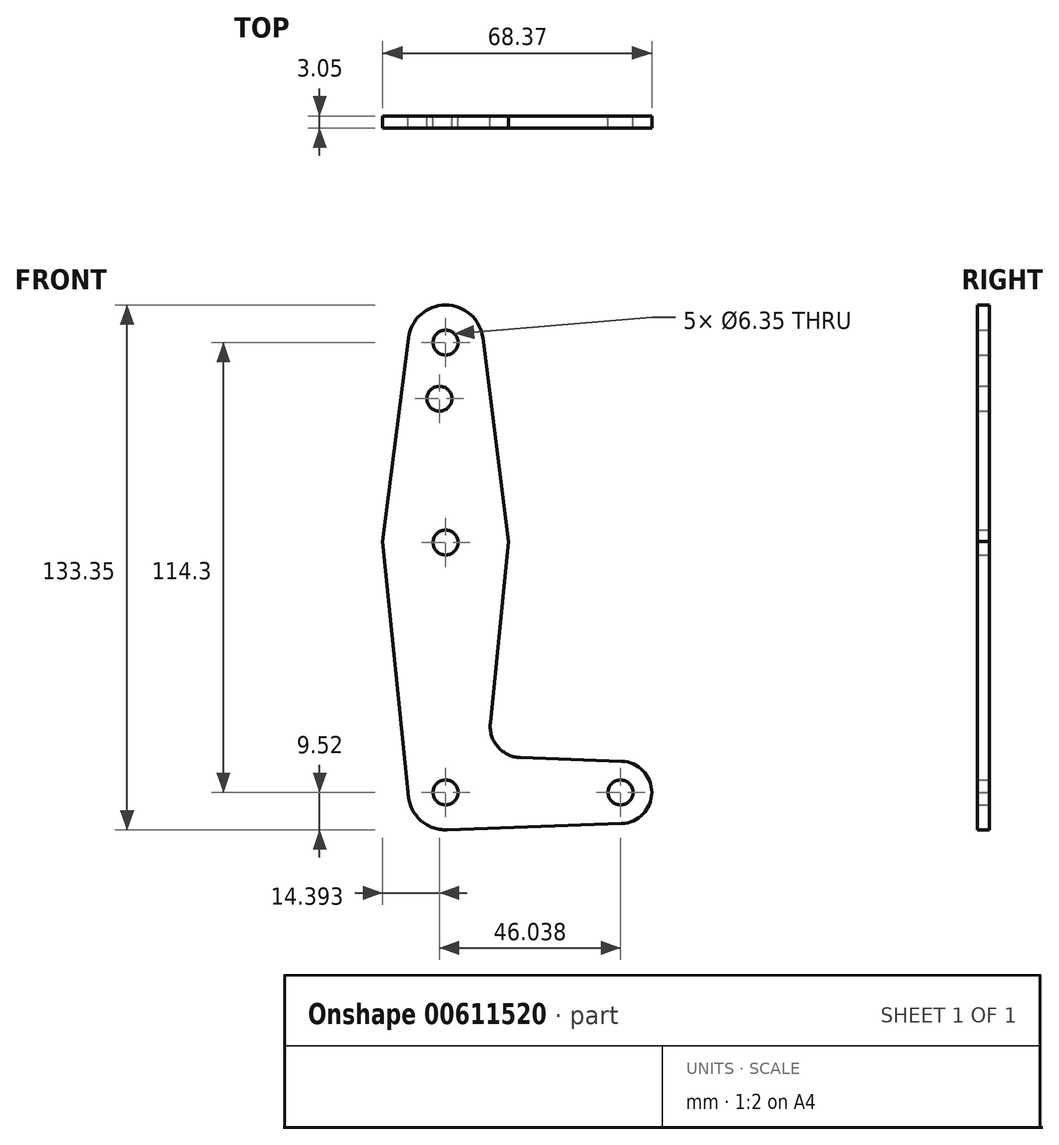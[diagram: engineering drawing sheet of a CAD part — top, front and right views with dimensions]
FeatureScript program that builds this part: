
annotation { "Feature Type Name" : "Feature", "Feature Type Description" : "" }
export const myFeature = defineFeature(function(context is Context, id is Id, definition is map)
    precondition{}
    {
        {
            var Q0;
            Q0=qCreatedBy(makeId("Front.planeOp"),FACE);
            var sketch = newSketch(context, id + "F0", { "sketchPlane" : qUnion([Q0])});
            skLineSegment(sketch, "E0", {"start": v(0, 0) * mm, "end": v(0, 114.3) * mm, "construction": true});
            skLineSegment(sketch, "E1", {"start": v(0, 0) * mm, "end": v(44.45, 0) * mm, "construction": true});
            skCircle(sketch, "E2", {"center": v(0, 114.3) * mm, "radius": 9.53 * mm});
            skCircle(sketch, "E3", {"center": v(0, 63.5) * mm, "radius": 15.88 * mm});
            skCircle(sketch, "E4", {"center": v(0, 0) * mm, "radius": 9.53 * mm});
            skCircle(sketch, "E5", {"center": v(44.45, 0) * mm, "radius": 7.94 * mm});
            skLineSegment(sketch, "E6", {"start": v(-9.45, 115.5) * mm, "end": v(-15.98, 63.7) * mm});
            skLineSegment(sketch, "E7", {"start": v(-15.98, 63.7) * mm, "end": v(-9.57, 0) * mm});
            skLineSegment(sketch, "E8", {"start": v(9.45, 115.5) * mm, "end": v(15.98, 63.7) * mm});
            skLineSegment(sketch, "E9", {"start": v(15.98, 63.7) * mm, "end": v(11.34, 17.6) * mm});
            skLineSegment(sketch, "E10", {"start": v(0, -9.53) * mm, "end": v(44.73, -7.93) * mm});
            skLineSegment(sketch, "E11", {"start": v(18.97, 8.85) * mm, "end": v(44.73, 7.93) * mm});
            skCircle(sketch, "E12", {"center": v(0, 114.3) * mm, "radius": 3.18 * mm});
            skCircle(sketch, "E13", {"center": v(0, 63.5) * mm, "radius": 3.18 * mm});
            skCircle(sketch, "E14", {"center": v(0, 0) * mm, "radius": 3.18 * mm});
            skCircle(sketch, "E15", {"center": v(44.45, 0) * mm, "radius": 3.18 * mm});
            skCircle(sketch, "E16", {"center": v(-1.59, 100.03) * mm, "radius": 3.18 * mm});
            skArc(sketch, "E17.filletArc", {"start": v(11.34, 17.6) * mm, "mid": v(13.26, 11.57) * mm, "end": v(18.97, 8.85) * mm});
            skLineSegment(sketch, "E18", {"start": v(-9.57, 0) * mm, "end": v(-9.53, 0) * mm});
            skSolve(sketch);
        }
        {
            var Q0;
            Q0 = qSketchRegion(id + "F0", true);
            extrude(context, id + "F1", {"entities" : qUnion([Q0]), "depth" : 3.05 * mm, "offsetDistance" : 25.4 * mm});
        }
    });
